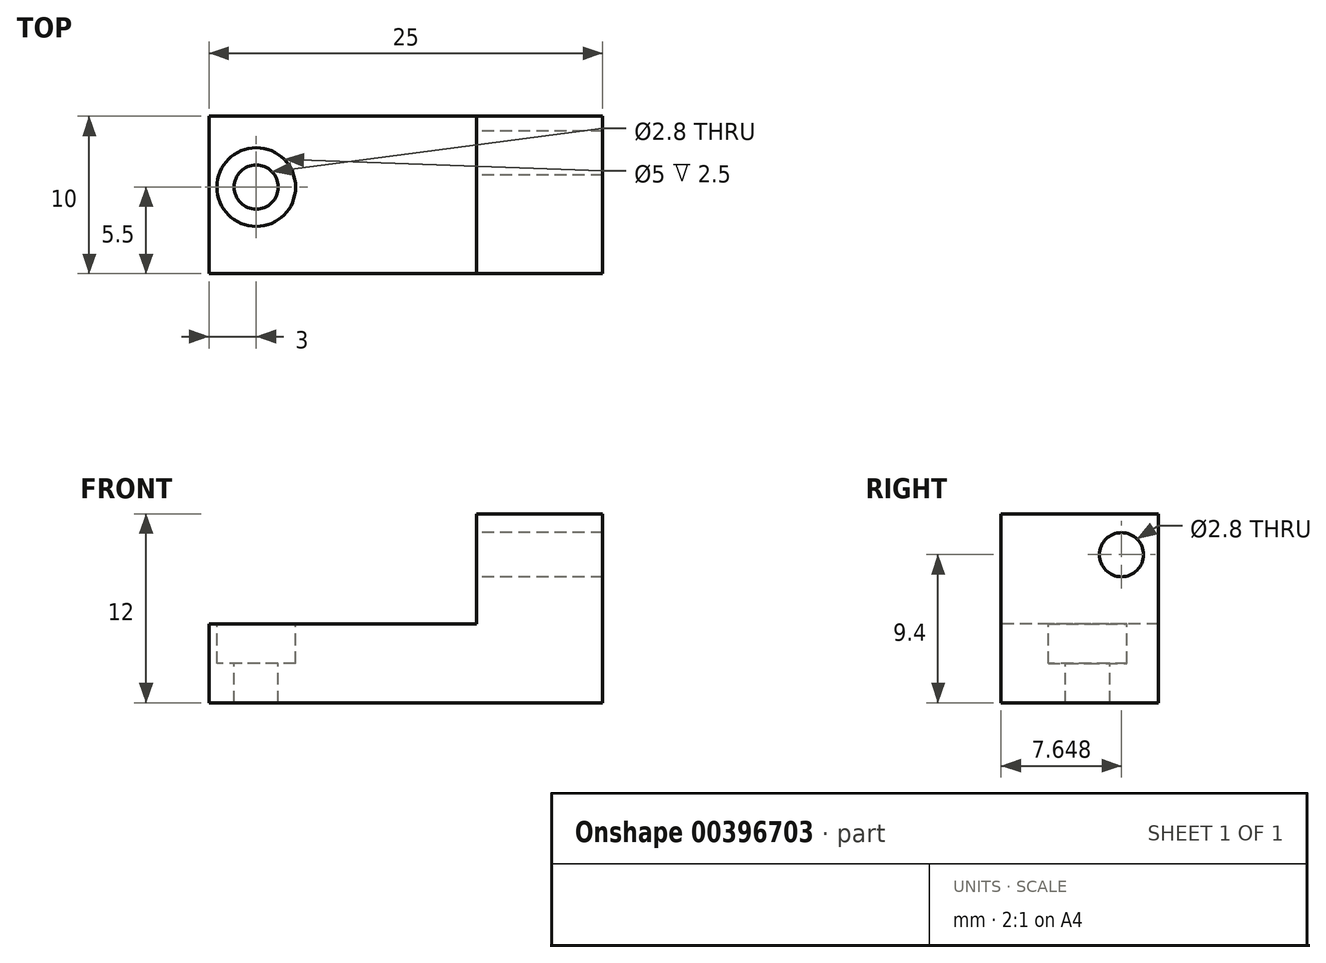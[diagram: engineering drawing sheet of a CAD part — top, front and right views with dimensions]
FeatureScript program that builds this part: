
annotation { "Feature Type Name" : "Feature", "Feature Type Description" : "" }
export const myFeature = defineFeature(function(context is Context, id is Id, definition is map)
    precondition{}
    {
        {
            var Q0;
            Q0=qCreatedBy(makeId("Top.planeOp"),FACE);
            var sketch = newSketch(context, id + "F0", { "sketchPlane" : qUnion([Q0])});
            skLineSegment(sketch, "E0.bottom", {"start": v(12.5, 5) * mm, "end": v(-12.5, 5) * mm});
            skLineSegment(sketch, "E0.top", {"start": v(12.5, -5) * mm, "end": v(-12.5, -5) * mm});
            skLineSegment(sketch, "E0.left", {"start": v(12.5, 5) * mm, "end": v(12.5, -5) * mm});
            skLineSegment(sketch, "E0.right", {"start": v(-12.5, 5) * mm, "end": v(-12.5, -5) * mm});
            skPoint(sketch, "E0.middle", {"position": v(0, 0) * mm});
            skSolve(sketch);
        }
        {
            var Q0;
            Q0=makeQuery(id+"F0.imprint","IMPRINT",FACE,{"disambiguationData":[TD([[makeQuery(id+"F0.imprint","IMPRINT",EDGE,{"derivedFrom":sQuery(id+"F0.wireOp",EDGE,"E0.bottom")}),1.0]])]});
            extrude(context, id + "F1", {"entities" : qUnion([Q0]), "depth" : 5 * mm});
        }
        {
            var Q0;
            Q0=makeQuery(id+"F1.opExtrude","CAP_FACE",FACE,{"disambiguationData":[OSD([sQuery(id+"F0.wireOp",EDGE,"E0.bottom"),sQuery(id+"F0.wireOp",EDGE,"E0.top"),sQuery(id+"F0.wireOp",EDGE,"E0.left"),sQuery(id+"F0.wireOp",EDGE,"E0.right")])],"isStart":false});
            var sketch = newSketch(context, id + "F2", { "sketchPlane" : qUnion([Q0])});
            skCircle(sketch, "E1", {"center": v(-9.5, 0.5) * mm, "radius": 1.4 * mm});
            skLineSegment(sketch, "E2", {"start": v(4.5, 5) * mm, "end": v(4.5, -5) * mm});
            skCircle(sketch, "E3", {"center": v(-9.5, 0.5) * mm, "radius": 2.5 * mm});
            skSolve(sketch);
        }
        {
            var Q0;
            Q0=makeQuery(id+"F2.imprint","IMPRINT",FACE,{"disambiguationData":[TD([[makeQuery(id+"F2.imprint","IMPRINT",EDGE,{"derivedFrom":sQuery(id+"F2.wireOp",EDGE,"E1")}),1.0]])]});
            extrude(context, id + "F3", {"entities" : qUnion([Q0]), "operationType" : NewBodyOperationType.REMOVE, "oppositeDirection" : true, "depth" : 25 * mm});
        }
        {
            var Q0;
            {var subQ0=sQuery(id+"F2.wireOp",EDGE,"E2");Q0=makeQuery(id+"F2.imprint","IMPRINT",FACE,{"disambiguationData":[TD([[makeQuery(id+"F2.imprint","IMPRINT",EDGE,{"derivedFrom":subQ0}),1.0]])]});}
            extrude(context, id + "F4", {"entities" : qUnion([Q0]), "operationType" : NewBodyOperationType.ADD, "depth" : 7 * mm});
        }
        {
            var Q0;
            Q0=makeQuery(id+"F4.opExtrude","SWEPT_FACE",FACE,{"disambiguationData":[OSD([sQuery(id+"F2.wireOp",EDGE,"E2")])]});
            var sketch = newSketch(context, id + "F5", { "sketchPlane" : qUnion([Q0])});
            skCircle(sketch, "E4", {"center": v(-2.65, 9.4) * mm, "radius": 1.4 * mm});
            skSolve(sketch);
        }
        {
            var Q0;
            Q0=makeQuery(id+"F5.imprint","IMPRINT",FACE,{"disambiguationData":[TD([[makeQuery(id+"F5.imprint","IMPRINT",EDGE,{"derivedFrom":sQuery(id+"F5.wireOp",EDGE,"E4")}),1.0]])]});
            extrude(context, id + "F6", {"entities" : qUnion([Q0]), "operationType" : NewBodyOperationType.REMOVE, "oppositeDirection" : true, "depth" : 25 * mm});
        }
        {
            var Q0;
            Q0=makeQuery(id+"F2.imprint","IMPRINT",FACE,{"disambiguationData":[TD([[makeQuery(id+"F2.imprint","IMPRINT",EDGE,{"derivedFrom":sQuery(id+"F2.wireOp",EDGE,"E1")}),-1.0]])]});
            extrude(context, id + "F7", {"entities" : qUnion([Q0]), "operationType" : NewBodyOperationType.REMOVE, "oppositeDirection" : true, "depth" : 2.5 * mm});
        }
    });
